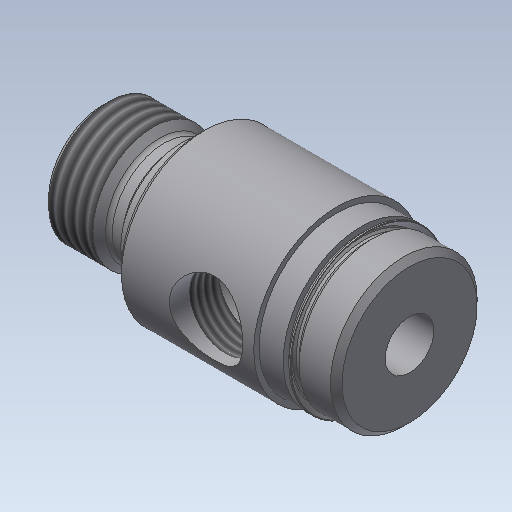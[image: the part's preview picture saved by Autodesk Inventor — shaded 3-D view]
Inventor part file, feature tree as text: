
AUTODESK INVENTOR PART (.ipt)
format: ipt  version: 2020 (Build 240168000, 168)  size: 327,680 bytes
history: native  units: in
note: dims shown in document units (in); Inventor stores cm internally (conversion verified against a paired STEP export)
features: other x119, sketch x6, revolve x5, thread x2, hole x1
ambient origin geometry x8: Origin, YZ Plane, XZ Plane, XY Plane, X Axis, Y Axis, Z Axis, Center Point
bodies: Solid1 (feature_tree)
feature tree (133):
  revolve  "Revolution1"  [1 undecoded]
  thread  "Thread1"  [1 undecoded]
  revolve  "Revolution2"  Angle=360.0deg
  hole  "Hole1"  [1 undecoded]
  revolve  "Revolution3"  [1 undecoded]
  revolve  "Revolution4"  [1 undecoded]
  thread  "Thread2"  [1 undecoded]
  revolve  "Revolution5"  [1 undecoded]
  other  "dp1_XY"
  other  "dp1_YZ"
  other  "dp1_ZX"
  other  "dp1_X"
  other  "dp1_Y"
  other  "dp1_Z"
  other  "dp1_Center"
  other  "dp2_XY"
  other  "dp2_YZ"
  other  "dp2_ZX"
  other  "dp2_X"
  other  "dp2_Y"
  other  "dp2_Z"
  other  "dp2_Center"
  other  "hh_XY"
  other  "hh_YZ"
  other  "hh_ZX"
  other  "hh_X"
  other  "hh_Y"
  other  "hh_Z"
  other  "hh_Center"
  other  "port_XY"
  other  "port_YZ"
  other  "port_ZX"
  other  "port_X"
  other  "port_Y"
  other  "port_Z"
  other  "port_Center"
  other  "rod_guide_XY"
  other  "rod_guide_YZ"
  other  "rod_guide_ZX"
  other  "rod_guide_X"
  other  "rod_guide_Y"
  other  "rod_guide_Z"
  other  "rod_guide_Center"
  other  "s1_XY"
  other  "s1_YZ"
  other  "s1_ZX"
  other  "s1_X"
  other  "s1_Y"
  other  "s1_Z"
  other  "s1_Center"
  other  "s2_XY"
  other  "s2_YZ"
  other  "s2_ZX"
  other  "s2_X"
  other  "s2_Y"
  other  "s2_Z"
  other  "s2_Center"
  other  "t1_XY"
  other  "t1_YZ"
  other  "t1_ZX"
  other  "t1_X"
  other  "t1_Y"
  other  "t1_Z"
  other  "t1_Center"
  other  "t111_XY"
  other  "t111_YZ"
  other  "t111_ZX"
  other  "t111_X"
  other  "t111_Y"
  other  "t111_Z"
  other  "t111_Center"
  other  "to_foot_bracket_XY"
  other  "to_foot_bracket_YZ"
  other  "to_foot_bracket_ZX"
  other  "to_foot_bracket_X"
  other  "to_foot_bracket_Y"
  other  "to_foot_bracket_Z"
  other  "to_foot_bracket_Center"
  other  "to_nut_XY"
  other  "to_nut_YZ"
  other  "to_nut_ZX"
  other  "to_nut_X"
  other  "to_nut_Y"
  other  "to_nut_Z"
  other  "to_nut_Center"
  other  "to_rod_XY"
  other  "to_rod_YZ"
  other  "to_rod_ZX"
  other  "to_rod_X"
  other  "to_rod_Y"
  other  "to_rod_Z"
  other  "to_rod_Center"
  other  "to_screw_XY"
  other  "to_screw_YZ"
  other  "to_screw_ZX"
  other  "to_screw_X"
  other  "to_screw_Y"
  other  "to_screw_Z"
  other  "to_screw_Center"
  other  "to_trunnion_brackets_XY"
  other  "to_trunnion_brackets_YZ"
  other  "to_trunnion_brackets_ZX"
  other  "to_trunnion_brackets_X"
  other  "to_trunnion_brackets_Y"
  other  "to_trunnion_brackets_Z"
  other  "to_trunnion_brackets_Center"
  other  "to_trunnion_brackets1_XY"
  other  "to_trunnion_brackets1_YZ"
  other  "to_trunnion_brackets1_ZX"
  other  "to_trunnion_brackets1_X"
  other  "to_trunnion_brackets1_Y"
  other  "to_trunnion_brackets1_Z"
  other  "to_trunnion_brackets1_Center"
  other  "to_trunnion_brackets2_XY"
  other  "to_trunnion_brackets2_YZ"
  other  "to_trunnion_brackets2_ZX"
  other  "to_trunnion_brackets2_X"
  other  "to_trunnion_brackets2_Y"
  other  "to_trunnion_brackets2_Z"
  other  "to_trunnion_brackets2_Center"
  other  "to_tube_XY"
  other  "to_tube_YZ"
  other  "to_tube_ZX"
  other  "to_tube_X"
  other  "to_tube_Y"
  other  "to_tube_Z"
  other  "to_tube_Center"
  sketch  "Sketch_2"  dims[d0=360.0deg d1=0.23in d2=0.0in d3=360.0deg]
  sketch  "Sketch_3"  dims[d4=0.2535in d5=0.75in d6=0.2735in d7=0.25in d8=90.0deg d9=1.594in d10=0.0in d11=360.0deg]
  sketch  "Sketch3"  dims[d12=360.0deg d13=0.1501in d14=0.0in]
  sketch  "Sketch_10"  dims[d15=360.0deg]
  sketch  "Sketch_40"  dims[d16=0.0in d17=0.0in d18=0.0in d19=0.0in d20=0.0in d21=0.0in]
  sketch  "Sketch_47"
note: 7 required parameter values undecoded (feature->parameter linkage not recoverable at this tier; creation-order binding heuristic only, values carry confidence <= 0.55)